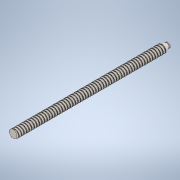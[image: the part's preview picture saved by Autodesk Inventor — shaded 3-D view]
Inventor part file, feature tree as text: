
AUTODESK INVENTOR PART (.ipt)
format: ipt  version: 2020.1 (Build 241239000, 239)  size: 3,648,000 bytes
history: native  units: mm
features: other x2, extrude x1, sketch x1
ambient origin geometry x8: Origin, YZ Plane, XZ Plane, XY Plane, X Axis, Y Axis, Z Axis, Center Point
bodies: Body1 (feature_tree)
feature tree (4):
  other  "Твердое тело1"
  extrude  "Выдавливание1"  Depth=100.0mm TaperAngle=0.0deg
  sketch  "Эскиз1"
  other  "Aesthetic Chamfer"
